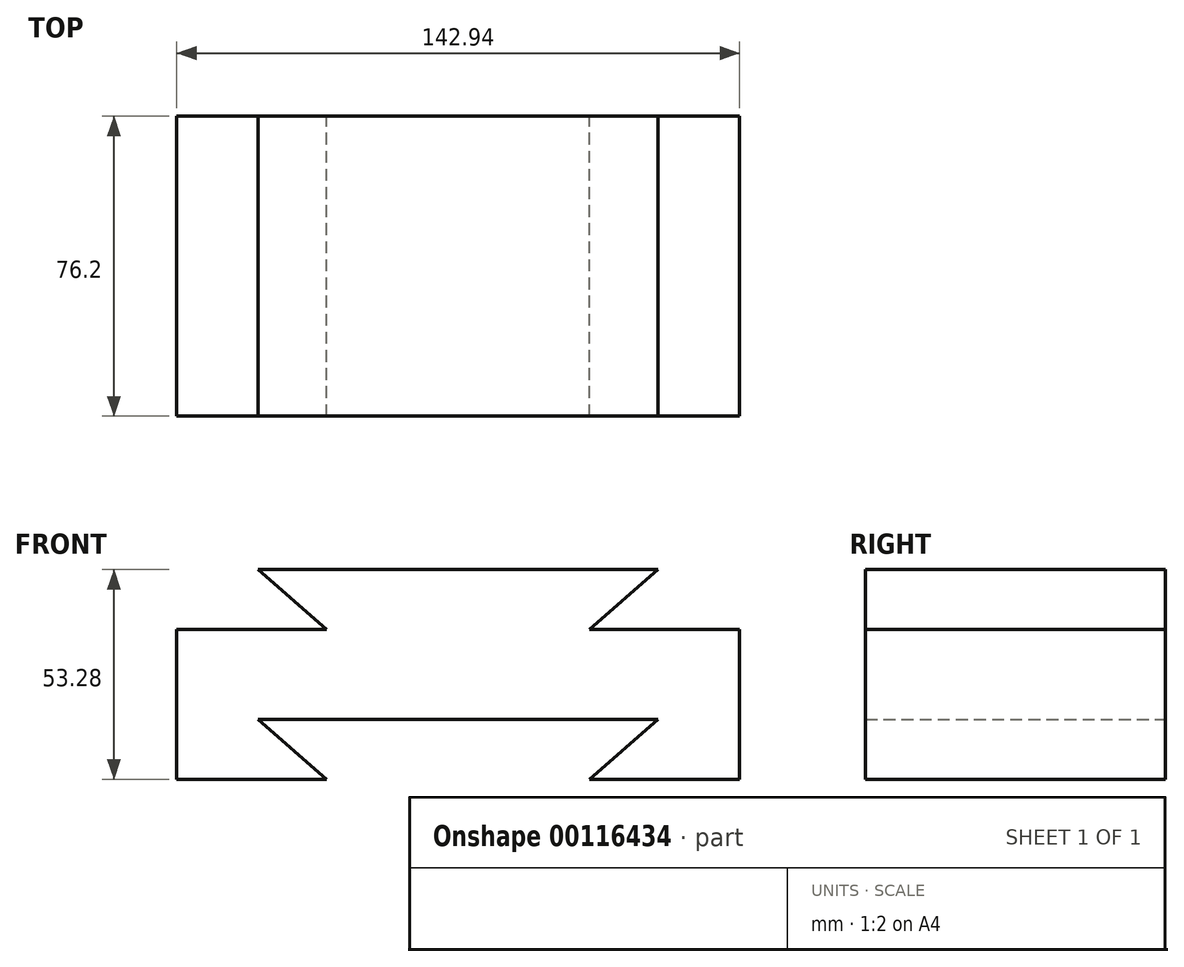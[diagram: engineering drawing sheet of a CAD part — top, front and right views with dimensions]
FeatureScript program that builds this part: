
annotation { "Feature Type Name" : "Feature", "Feature Type Description" : "" }
export const myFeature = defineFeature(function(context is Context, id is Id, definition is map)
    precondition{}
    {
        {
            var Q0;
            Q0=qCreatedBy(makeId("Front.planeOp"),FACE);
            var sketch = newSketch(context, id + "F0", { "sketchPlane" : qUnion([Q0])});
            skLineSegment(sketch, "E0", {"start": v(0, 0) * mm, "end": v(0, 38.1) * mm});
            skLineSegment(sketch, "E1", {"start": v(0, 38.1) * mm, "end": v(-38.1, 38.1) * mm});
            skLineSegment(sketch, "E2", {"start": v(0, 0) * mm, "end": v(-38.1, 0) * mm});
            skLineSegment(sketch, "E3", {"start": v(-38.1, 0) * mm, "end": v(-20.67, 15.18) * mm});
            skLineSegment(sketch, "E4", {"start": v(-20.67, 15.18) * mm, "end": v(-122.27, 15.18) * mm});
            skLineSegment(sketch, "E5", {"start": v(-122.27, 15.18) * mm, "end": v(-104.84, 0) * mm});
            skLineSegment(sketch, "E6", {"start": v(-104.84, 0) * mm, "end": v(-142.94, 0) * mm});
            skLineSegment(sketch, "E7", {"start": v(-142.94, 0) * mm, "end": v(-142.94, 38.1) * mm});
            skLineSegment(sketch, "E8", {"start": v(-142.94, 38.1) * mm, "end": v(-104.84, 38.1) * mm});
            skLineSegment(sketch, "E9", {"start": v(-104.84, 38.1) * mm, "end": v(-122.27, 53.28) * mm});
            skLineSegment(sketch, "E10", {"start": v(-122.27, 53.28) * mm, "end": v(-20.67, 53.28) * mm});
            skLineSegment(sketch, "E11", {"start": v(-20.67, 53.28) * mm, "end": v(-38.1, 38.1) * mm});
            skSolve(sketch);
        }
        {
            var Q0;
            Q0=makeQuery(id+"F0.imprint","IMPRINT",FACE,{"disambiguationData":[TD([[makeQuery(id+"F0.imprint","IMPRINT",EDGE,{"derivedFrom":sQuery(id+"F0.wireOp",EDGE,"E0")}),1.0]])]});
            extrude(context, id + "F1", {"entities" : qUnion([Q0]), "depth" : 76.2 * mm});
        }
    });
